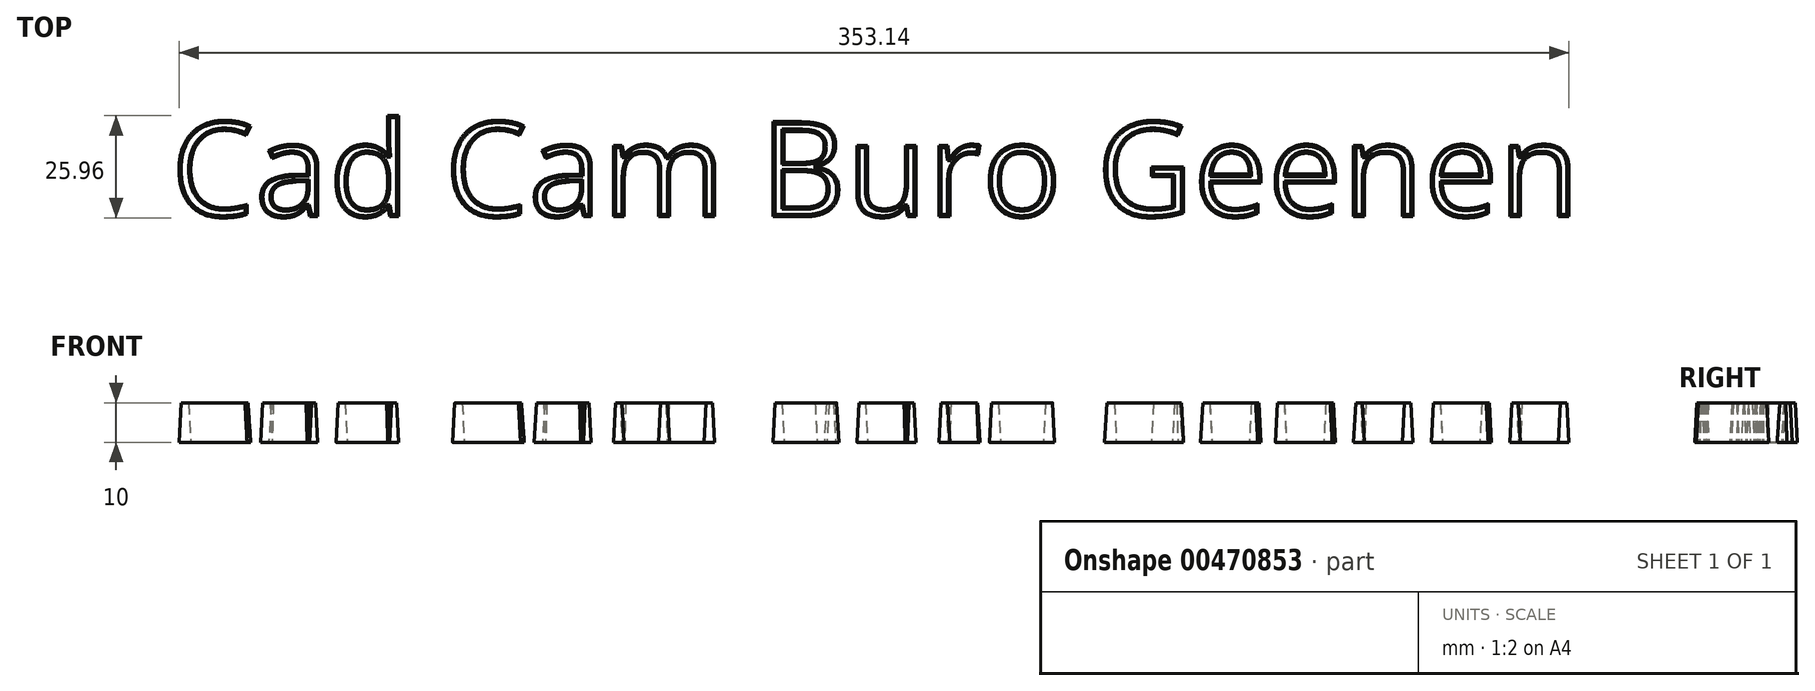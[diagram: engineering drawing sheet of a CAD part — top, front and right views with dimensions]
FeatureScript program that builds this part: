
annotation { "Feature Type Name" : "Feature", "Feature Type Description" : "" }
export const myFeature = defineFeature(function(context is Context, id is Id, definition is map)
    precondition{}
    {
        {
            var Q0;
            Q0=qCreatedBy(makeId("Top.planeOp"),FACE);
            var sketch = newSketch(context, id + "F0", { "sketchPlane" : qUnion([Q0])});
            skText(sketch, "E0", { "text": "Cad Cam Buro Geenen", "fontName": "OpenSans-Regular.ttf"});
            const initialGuessF0  = {"E0": [0.07379, 0.05232, 1, 0, 0.02429]};
            skSetInitialGuess(sketch, initialGuessF0);
            skSolve(sketch);
        }
        {
            var Q0;
            Q0 = qSketchRegion(id + "F0", true);
            extrude(context, id + "F1", {"entities" : qUnion([Q0]), "depth" : 10 * mm, "hasDraft" : true, "draftAngle" : 3 * degree, "draftPullDirection" : true});
        }
    });
